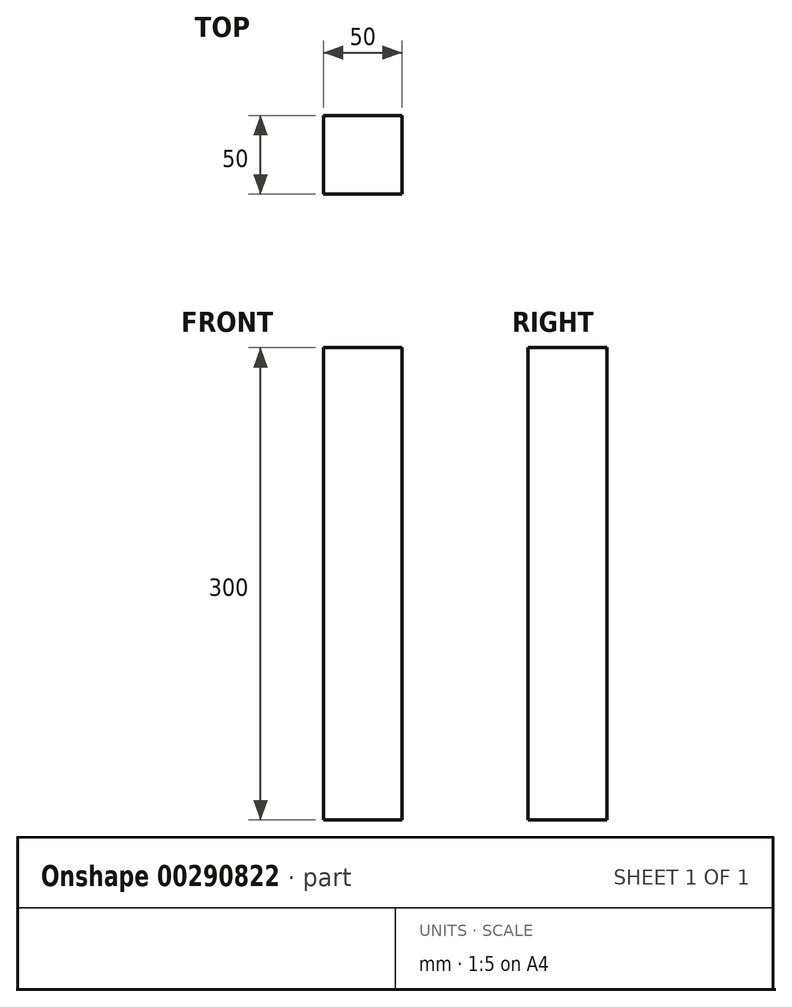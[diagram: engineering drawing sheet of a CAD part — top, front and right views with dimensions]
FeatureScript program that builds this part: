
annotation { "Feature Type Name" : "Feature", "Feature Type Description" : "" }
export const myFeature = defineFeature(function(context is Context, id is Id, definition is map)
    precondition{}
    {
        {
            var Q0;
            Q0=qCreatedBy(makeId("Top.planeOp"),FACE);
            var sketch = newSketch(context, id + "F0", { "sketchPlane" : qUnion([Q0])});
            skLineSegment(sketch, "E0.bottom", {"start": v(25, 25) * mm, "end": v(-25, 25) * mm});
            skLineSegment(sketch, "E0.top", {"start": v(25, -25) * mm, "end": v(-25, -25) * mm});
            skLineSegment(sketch, "E0.left", {"start": v(25, 25) * mm, "end": v(25, -25) * mm});
            skLineSegment(sketch, "E0.right", {"start": v(-25, 25) * mm, "end": v(-25, -25) * mm});
            skPoint(sketch, "E0.middle", {"position": v(0, 0) * mm});
            skSolve(sketch);
        }
        {
            var Q0;
            Q0=makeQuery(id+"F0.imprint","IMPRINT",FACE,{"disambiguationData":[TD([[makeQuery(id+"F0.imprint","IMPRINT",EDGE,{"derivedFrom":sQuery(id+"F0.wireOp",EDGE,"E0.bottom")}),1.0]])]});
            extrude(context, id + "F1", {"entities" : qUnion([Q0]), "depth" : 300 * mm});
        }
    });
